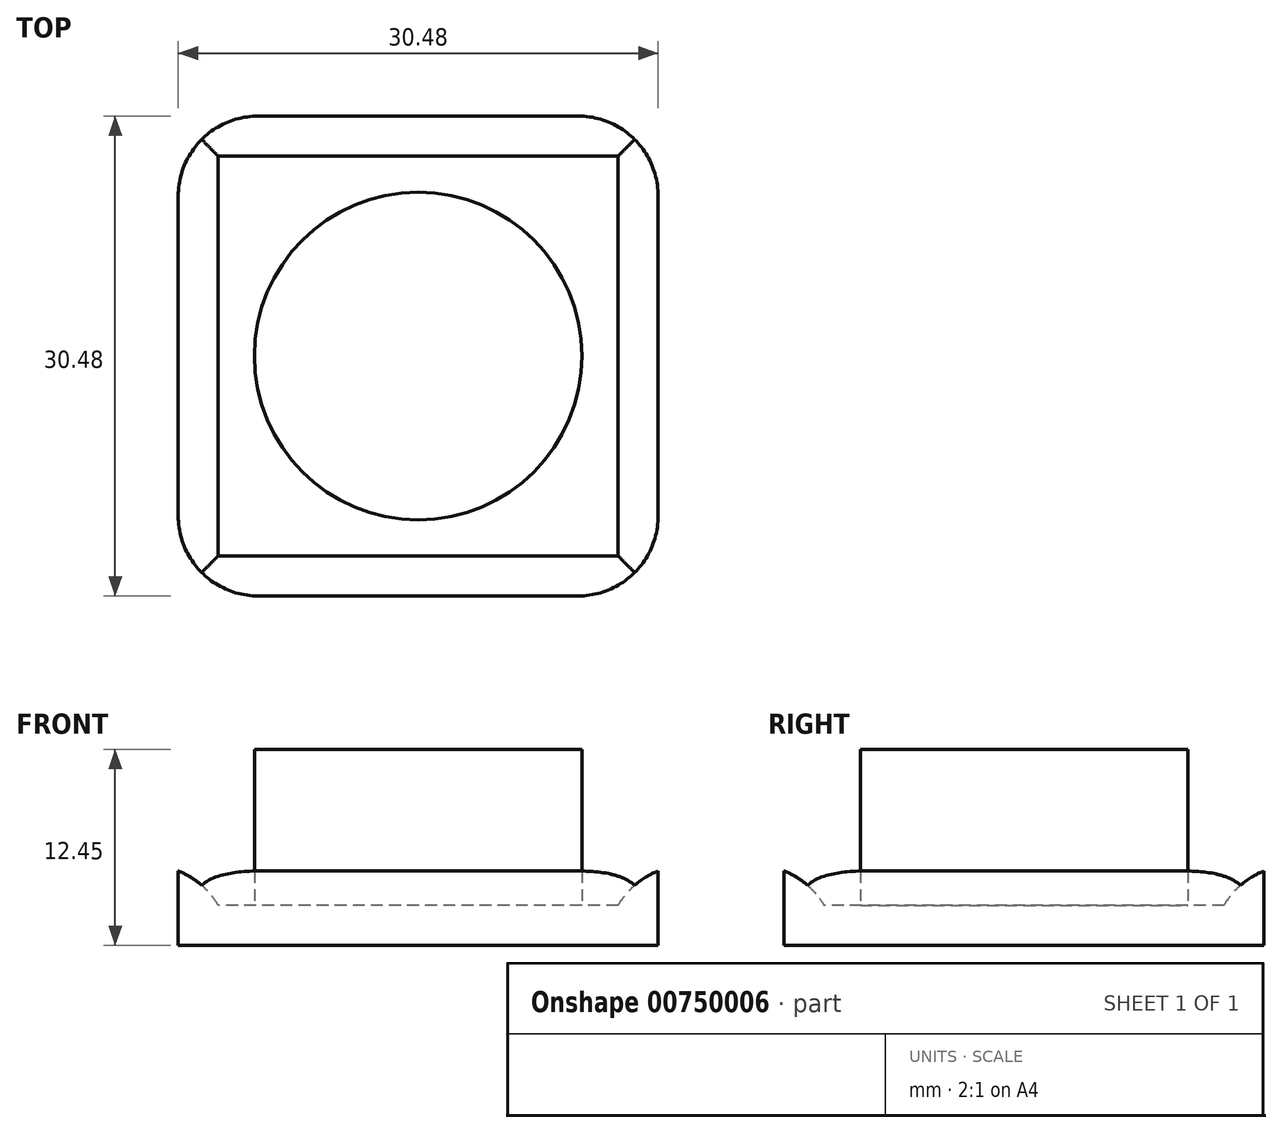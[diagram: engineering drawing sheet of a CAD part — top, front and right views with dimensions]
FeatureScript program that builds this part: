
annotation { "Feature Type Name" : "Feature", "Feature Type Description" : "" }
export const myFeature = defineFeature(function(context is Context, id is Id, definition is map)
    precondition{}
    {
        {
            var Q0;
            Q0=qCreatedBy(makeId("Top.planeOp"),FACE);
            var sketch = newSketch(context, id + "F0", { "sketchPlane" : qUnion([Q0])});
            skLineSegment(sketch, "E0.bottom", {"start": v(15.24, 15.24) * mm, "end": v(-15.24, 15.24) * mm});
            skLineSegment(sketch, "E0.top", {"start": v(15.24, -15.24) * mm, "end": v(-15.24, -15.24) * mm});
            skLineSegment(sketch, "E0.left", {"start": v(15.24, 15.24) * mm, "end": v(15.24, -15.24) * mm});
            skLineSegment(sketch, "E0.right", {"start": v(-15.24, 15.24) * mm, "end": v(-15.24, -15.24) * mm});
            skPoint(sketch, "E0.middle", {"position": v(0, 0) * mm});
            skSolve(sketch);
        }
        {
            var Q0;
            Q0=makeQuery(id+"F0.imprint","IMPRINT",FACE,{"disambiguationData":[TD([[makeQuery(id+"F0.imprint","IMPRINT",EDGE,{"derivedFrom":sQuery(id+"F0.wireOp",EDGE,"E0.bottom")}),1.0]])]});
            extrude(context, id + "F1", {"entities" : qUnion([Q0]), "depth" : 5.08 * mm, "offsetDistance" : 25.4 * mm});
        }
        {
            var Q0;
            Q0=makeQuery(id+"F1.opExtrude","CAP_FACE",FACE,{"disambiguationData":[OSD([sQuery(id+"F0.wireOp",EDGE,"E0.bottom"),sQuery(id+"F0.wireOp",EDGE,"E0.top"),sQuery(id+"F0.wireOp",EDGE,"E0.left"),sQuery(id+"F0.wireOp",EDGE,"E0.right")])],"isStart":false});
            shell(context, id + "F2", {"entities" : qUnion([Q0]), "thickness" : 2.54 * mm});
        }
        {
            var Q0;
            {var subQ0=sQuery(id+"F0.wireOp",EDGE,"E0.bottom");Q0=makeQuery(id+"F2.opShell","OFFSET_EDGE",EDGE,{"disambiguationData":[OSD([subQ0]),TDD([makeQuery(id+"F1.opExtrude","CAP_EDGE",EDGE,{"disambiguationData":[OSD([subQ0])],"isStart":false})])]});}
            var Q1;
            {var subQ0=sQuery(id+"F0.wireOp",EDGE,"E0.left");Q1=makeQuery(id+"F2.opShell","OFFSET_EDGE",EDGE,{"disambiguationData":[OSD([subQ0]),TDD([makeQuery(id+"F1.opExtrude","CAP_EDGE",EDGE,{"disambiguationData":[OSD([subQ0])],"isStart":false})])]});}
            var Q2;
            {var subQ0=sQuery(id+"F0.wireOp",EDGE,"E0.top");Q2=makeQuery(id+"F2.opShell","OFFSET_EDGE",EDGE,{"disambiguationData":[OSD([subQ0]),TDD([makeQuery(id+"F1.opExtrude","CAP_EDGE",EDGE,{"disambiguationData":[OSD([subQ0])],"isStart":false})])]});}
            var Q3;
            {var subQ0=sQuery(id+"F0.wireOp",EDGE,"E0.right");Q3=makeQuery(id+"F2.opShell","OFFSET_EDGE",EDGE,{"disambiguationData":[OSD([subQ0]),TDD([makeQuery(id+"F1.opExtrude","CAP_EDGE",EDGE,{"disambiguationData":[OSD([subQ0])],"isStart":false})])]});}
            fillet(context, id + "F3", {"entities" : qUnion([Q0, Q1, Q2, Q3]), "radius" : 5.08 * mm, "tangentPropagation" : true, "allowEdgeOverflow" : false});
        }
        {
            var Q0;
            Q0=makeQuery(id+"F1.opExtrude","SWEPT_EDGE",EDGE,{"disambiguationData":[OSD([sQuery(id+"F0.wireOp",EDGE,"E0.top"),sQuery(id+"F0.wireOp",EDGE,"E0.left")])]});
            var Q1;
            Q1=makeQuery(id+"F1.opExtrude","SWEPT_EDGE",EDGE,{"disambiguationData":[OSD([sQuery(id+"F0.wireOp",EDGE,"E0.top"),sQuery(id+"F0.wireOp",EDGE,"E0.right")])]});
            var Q2;
            Q2=makeQuery(id+"F1.opExtrude","SWEPT_EDGE",EDGE,{"disambiguationData":[OSD([sQuery(id+"F0.wireOp",EDGE,"E0.bottom"),sQuery(id+"F0.wireOp",EDGE,"E0.left")])]});
            var Q3;
            Q3=makeQuery(id+"F1.opExtrude","SWEPT_EDGE",EDGE,{"disambiguationData":[OSD([sQuery(id+"F0.wireOp",EDGE,"E0.bottom"),sQuery(id+"F0.wireOp",EDGE,"E0.right")])]});
            fillet(context, id + "F4", {"entities" : qUnion([Q0, Q1, Q2, Q3]), "radius" : 5.08 * mm, "tangentPropagation" : true, "allowEdgeOverflow" : false});
        }
        {
            var Q0;
            Q0=qCreatedBy(makeId("Top.planeOp"),FACE);
            var sketch = newSketch(context, id + "F5", { "sketchPlane" : qUnion([Q0])});
            skCircle(sketch, "E1", {"center": v(0, 0) * mm, "radius": 10.4 * mm});
            skSolve(sketch);
        }
        {
            var Q0;
            Q0 = qSketchRegion(id + "F5", true);
            extrude(context, id + "F6", {"entities" : qUnion([Q0]), "operationType" : NewBodyOperationType.ADD, "depth" : 12.45 * mm, "offsetDistance" : 25.4 * mm});
        }
    });
